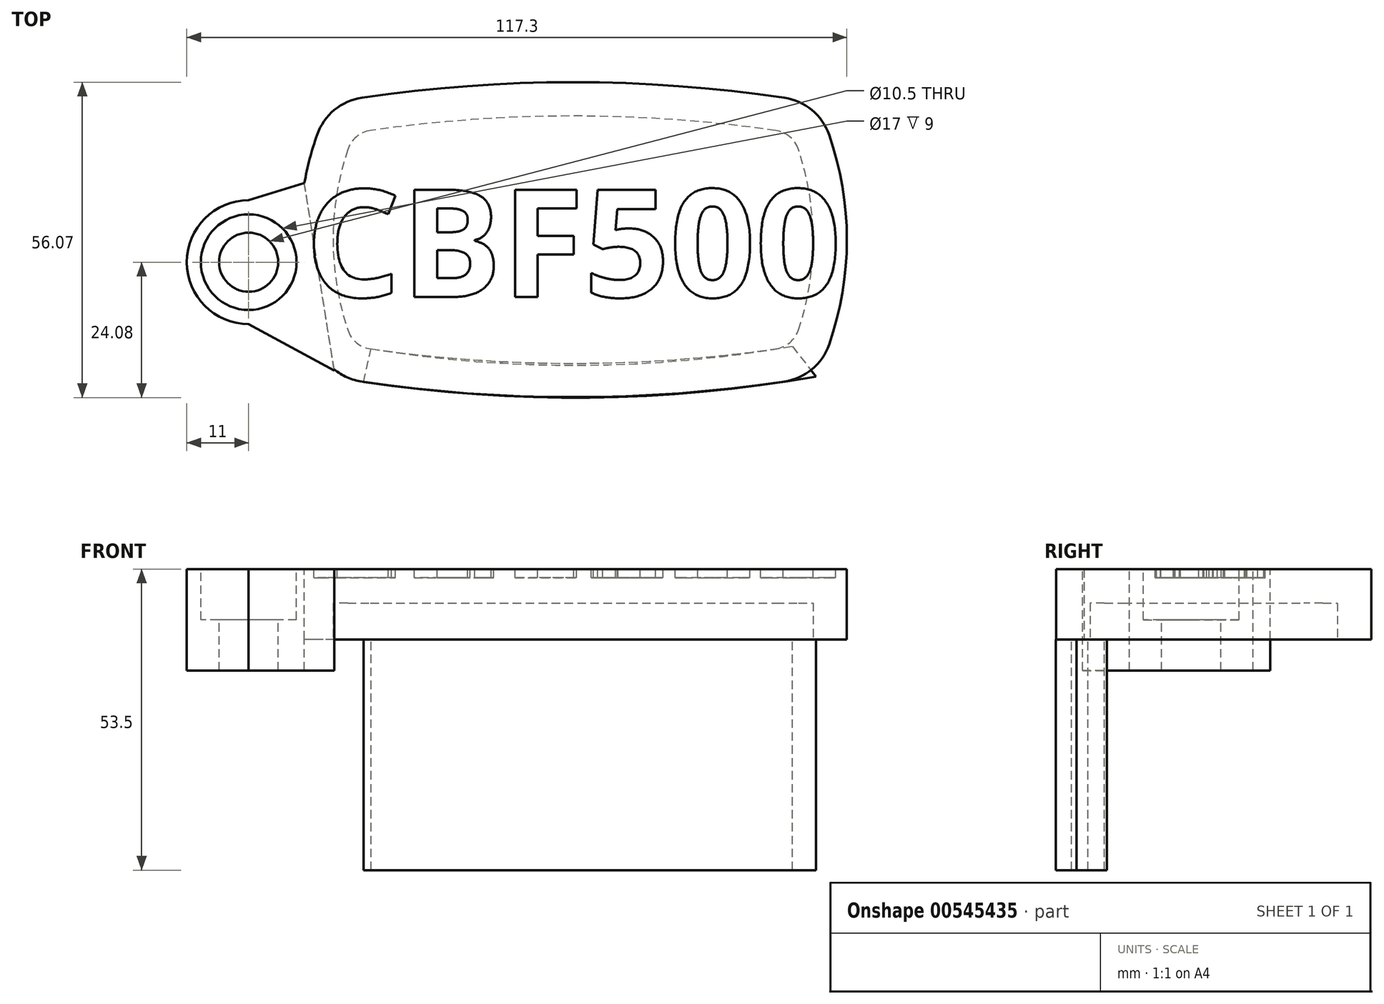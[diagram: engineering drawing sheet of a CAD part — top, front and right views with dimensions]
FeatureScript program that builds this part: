
annotation { "Feature Type Name" : "Feature", "Feature Type Description" : "" }
export const myFeature = defineFeature(function(context is Context, id is Id, definition is map)
    precondition{}
    {
        {
            var Q0;
            Q0=qCreatedBy(makeId("Top.planeOp"),FACE);
            var sketch = newSketch(context, id + "F0", { "sketchPlane" : qUnion([Q0])});
            skArc(sketch, "E0", {"start": v(0, 0) * mm, "mid": v(5.5, 24.35) * mm, "end": v(0, 48.7) * mm});
            skArc(sketch, "E1", {"start": v(-86.3, 0) * mm, "mid": v(-43.15, -3.64) * mm, "end": v(0, 0) * mm});
            skPoint(sketch, "E2", {"position": v(-43.15, 0) * mm});
            skPoint(sketch, "E3", {"position": v(0, 24.35) * mm});
            skLineSegment(sketch, "E4", {"start": v(-43.15, 0) * mm, "end": v(-43.15, 43.73) * mm, "construction": true});
            skLineSegment(sketch, "E5", {"start": v(0, 24.35) * mm, "end": v(-27.75, 24.35) * mm, "construction": true});
            skArc(sketch, "E6.MirrorCS", {"start": v(-86.3, 48.7) * mm, "mid": v(-43.15, 52.34) * mm, "end": v(0, 48.7) * mm});
            skArc(sketch, "E7.MirrorCS", {"start": v(-86.3, 0) * mm, "mid": v(-91.8, 24.35) * mm, "end": v(-86.3, 48.7) * mm});
            skSolve(sketch);
        }
        {
            var Q0;
            Q0 = qSketchRegion(id + "F0", true);
            extrude(context, id + "F1", {"entities" : qUnion([Q0]), "depth" : 12.5 * mm, "offsetDistance" : 25 * mm});
        }
        {
            var Q0;
            Q0=makeQuery(id+"F1.opExtrude","CAP_FACE",FACE,{"disambiguationData":[OSD([sQuery(id+"F0.wireOp",EDGE,"E0"),sQuery(id+"F0.wireOp",EDGE,"E1"),sQuery(id+"F0.wireOp",EDGE,"E6.MirrorCS"),sQuery(id+"F0.wireOp",EDGE,"E7.MirrorCS")])],"isStart":true});
            shell(context, id + "F2", {"entities" : qUnion([Q0]), "thickness" : 6 * mm});
        }
        {
            var Q0;
            Q0=makeQuery(id+"F1.opExtrude","CAP_FACE",FACE,{"disambiguationData":[OSD([sQuery(id+"F0.wireOp",EDGE,"E0"),sQuery(id+"F0.wireOp",EDGE,"E1"),sQuery(id+"F0.wireOp",EDGE,"E6.MirrorCS"),sQuery(id+"F0.wireOp",EDGE,"E7.MirrorCS")])],"isStart":true});
            var sketch = newSketch(context, id + "F3", { "sketchPlane" : qUnion([Q0])});
            skLineSegment(sketch, "E8", {"start": v(-4.18, -5.4) * mm, "end": v(0, 0) * mm});
            skLineSegment(sketch, "E9", {"start": v(-80.38, 0.94) * mm, "end": v(-79.02, -4.93) * mm});
            skArc(sketch, "E10", {"start": v(0, 0) * mm, "mid": v(-40.15, 3.72) * mm, "end": v(-80.38, 0.94) * mm});
            skArc(sketch, "E11", {"start": v(-4.18, -5.4) * mm, "mid": v(-41.58, -2.03) * mm, "end": v(-79.02, -4.93) * mm});
            skSolve(sketch);
        }
        {
            var Q0;
            Q0=makeQuery(id+"F1.opExtrude","SWEPT_EDGE",EDGE,{"disambiguationData":[OSD([sQuery(id+"F0.wireOp",EDGE,"E0"),sQuery(id+"F0.wireOp",EDGE,"E6.MirrorCS")])]});
            var Q1;
            Q1=makeQuery(id+"F1.opExtrude","SWEPT_EDGE",EDGE,{"disambiguationData":[OSD([sQuery(id+"F0.wireOp",EDGE,"E0"),sQuery(id+"F0.wireOp",EDGE,"E1")])]});
            var Q2;
            Q2=makeQuery(id+"F1.opExtrude","SWEPT_EDGE",EDGE,{"disambiguationData":[OSD([sQuery(id+"F0.wireOp",EDGE,"E1"),sQuery(id+"F0.wireOp",EDGE,"E7.MirrorCS")])]});
            var Q3;
            Q3=makeQuery(id+"F1.opExtrude","SWEPT_EDGE",EDGE,{"disambiguationData":[OSD([sQuery(id+"F0.wireOp",EDGE,"E6.MirrorCS"),sQuery(id+"F0.wireOp",EDGE,"E7.MirrorCS")])]});
            fillet(context, id + "F4", {"entities" : qUnion([Q0, Q1, Q2, Q3]), "radius" : 10 * mm, "tangentPropagation" : true, "allowEdgeOverflow" : false});
        }
        {
            var Q0;
            Q0 = qSketchRegion(id + "F3", true);
            extrude(context, id + "F5", {"entities" : qUnion([Q0]), "operationType" : NewBodyOperationType.ADD, "depth" : 31.6 * mm, "offsetDistance" : 25 * mm});
        }
        {
            var Q0;
            Q0=qCreatedBy(makeId("Front.planeOp"),FACE);
            var sketch = newSketch(context, id + "F6", { "sketchPlane" : qUnion([Q0])});
            skLineSegment(sketch, "E12", {"start": v(-60.38, -32) * mm, "end": v(-80.38, -32) * mm});
            skLineSegment(sketch, "E13", {"start": v(-80.38, -32) * mm, "end": v(-80.38, 0) * mm});
            skLineSegment(sketch, "E14", {"start": v(-80.38, 0) * mm, "end": v(-60.38, -32) * mm});
            skSolve(sketch);
        }
        {
            var Q0;
            Q0 = qSketchRegion(id + "F6", true);
            extrude(context, id + "F7", {"entities" : qUnion([Q0]), "operationType" : NewBodyOperationType.REMOVE, "oppositeDirection" : true, "depth" : 25 * mm, "offsetDistance" : 25 * mm, "hasSecondDirection" : true, "secondDirectionOppositeDirection" : false, "secondDirectionDepth" : 25 * mm});
        }
        {
            var Q0;
            Q0=makeQuery(id+"F5.opExtrude","SWEPT_EDGE",EDGE,{"disambiguationData":[OSD([sQuery(id+"F0.wireOp",EDGE,"E0"),sQuery(id+"F0.wireOp",EDGE,"E1"),sQuery(id+"F3.wireOp",EDGE,"E8"),sQuery(id+"F3.wireOp",EDGE,"2BGsfKZn-jyZl-Ejkt-ld0F-ZE4WbALv0zhB")])]});
            fillet(context, id + "F8", {"entities" : qUnion([Q0]), "radius" : 2 * mm, "tangentPropagation" : true, "allowEdgeOverflow" : false});
        }
        {
            var Q0;
            Q0=qCreatedBy(makeId("Front.planeOp"),FACE);
            var sketch = newSketch(context, id + "F9", { "sketchPlane" : qUnion([Q0])});
            skLineSegment(sketch, "E15", {"start": v(-1.05, -32) * mm, "end": v(-1.05, -16) * mm});
            skLineSegment(sketch, "E16", {"start": v(-1.05, -16) * mm, "end": v(-17.05, -32.07) * mm});
            skLineSegment(sketch, "E17", {"start": v(-17.05, -32.07) * mm, "end": v(-1.05, -32) * mm});
            skSolve(sketch);
        }
        {
            var Q0;
            Q0 = qSketchRegion(id + "F9", true);
            extrude(context, id + "F10", {"entities" : qUnion([Q0]), "operationType" : NewBodyOperationType.REMOVE, "oppositeDirection" : true, "depth" : 25 * mm, "offsetDistance" : 25 * mm, "hasSecondDirection" : true, "secondDirectionOppositeDirection" : false, "secondDirectionDepth" : 25 * mm});
        }
        {
            var Q0;
            Q0=makeQuery(id+"F1.opExtrude","CAP_FACE",FACE,{"disambiguationData":[OSD([sQuery(id+"F0.wireOp",EDGE,"E0"),sQuery(id+"F0.wireOp",EDGE,"E1"),sQuery(id+"F0.wireOp",EDGE,"E6.MirrorCS"),sQuery(id+"F0.wireOp",EDGE,"E7.MirrorCS")])],"isStart":false});
            var sketch = newSketch(context, id + "F11", { "sketchPlane" : qUnion([Q0])});
            skCircle(sketch, "E18", {"center": v(-100.8, 20.35) * mm, "radius": 5.25 * mm});
            skArc(sketch, "E19", {"start": v(-100.8, 31.35) * mm, "mid": v(-111.8, 20.35) * mm, "end": v(-100.8, 9.35) * mm});
            skLineSegment(sketch, "E20", {"start": v(-100.8, 31.35) * mm, "end": v(-90.9, 34.4) * mm});
            skLineSegment(sketch, "E21", {"start": v(-100.8, 9.35) * mm, "end": v(-85.57, 1.08) * mm});
            skPoint(sketch, "E21.endSnap0", {"position": v(-85.57, 1.3) * mm});
            skLineSegment(sketch, "E22", {"start": v(-85.57, 1.08) * mm, "end": v(-90.9, 34.4) * mm});
            skSolve(sketch);
        }
        {
            var Q0;
            Q0 = qSketchRegion(id + "F11", true);
            extrude(context, id + "F12", {"entities" : qUnion([Q0]), "operationType" : NewBodyOperationType.ADD, "oppositeDirection" : true, "depth" : 18 * mm, "offsetDistance" : 25 * mm});
        }
        {
            var Q0;
            Q0=makeQuery(id+"F12.boolean.opBoolean","MERGE",FACE,{"derivedFrom":[makeQuery(id+"F1.opExtrude","CAP_FACE",FACE,{"disambiguationData":[OSD([sQuery(id+"F0.wireOp",EDGE,"E0"),sQuery(id+"F0.wireOp",EDGE,"E1"),sQuery(id+"F0.wireOp",EDGE,"E6.MirrorCS"),sQuery(id+"F0.wireOp",EDGE,"E7.MirrorCS")])],"isStart":false}),makeQuery(id+"F12.opExtrude","CAP_FACE",FACE,{"disambiguationData":[OSD([sQuery(id+"F11.wireOp",EDGE,"E18"),sQuery(id+"F11.wireOp",EDGE,"E19"),sQuery(id+"F11.wireOp",EDGE,"E20"),sQuery(id+"F11.wireOp",EDGE,"Zz5zplqs-EO2A-KGeE-ttNv-1fYVzeMaVuvq"),sQuery(id+"F11.wireOp",EDGE,"bp7XOPkl-K0a4-XZaF-Fh4k-H6mTY0HdMkWh")])],"isStart":true})]});
            var sketch = newSketch(context, id + "F13", { "sketchPlane" : qUnion([Q0])});
            skCircle(sketch, "E23", {"center": v(-100.8, 20.35) * mm, "radius": 8.5 * mm});
            skSolve(sketch);
        }
        {
            var Q0;
            Q0 = qSketchRegion(id + "F13", true);
            extrude(context, id + "F14", {"entities" : qUnion([Q0]), "operationType" : NewBodyOperationType.REMOVE, "oppositeDirection" : true, "depth" : 9 * mm, "offsetDistance" : 25 * mm});
        }
        {
            var Q0;
            Q0=makeQuery(id+"F2.opShell","OFFSET_EDGE",EDGE,{"disambiguationData":[OSD([sQuery(id+"F0.wireOp",EDGE,"E0"),sQuery(id+"F0.wireOp",EDGE,"E6.MirrorCS")])]});
            var Q1;
            Q1=makeQuery(id+"F2.opShell","OFFSET_EDGE",EDGE,{"disambiguationData":[OSD([sQuery(id+"F0.wireOp",EDGE,"E6.MirrorCS"),sQuery(id+"F0.wireOp",EDGE,"E7.MirrorCS")])]});
            var Q2;
            Q2=makeQuery(id+"F2.opShell","OFFSET_EDGE",EDGE,{"disambiguationData":[OSD([sQuery(id+"F0.wireOp",EDGE,"E1"),sQuery(id+"F0.wireOp",EDGE,"E7.MirrorCS")])]});
            var Q3;
            Q3=makeQuery(id+"F2.opShell","OFFSET_EDGE",EDGE,{"disambiguationData":[OSD([sQuery(id+"F0.wireOp",EDGE,"E0"),sQuery(id+"F0.wireOp",EDGE,"E1")])]});
            fillet(context, id + "F15", {"entities" : qUnion([Q0, Q1, Q2, Q3]), "radius" : 5 * mm, "tangentPropagation" : true, "allowEdgeOverflow" : false});
        }
        {
            var Q0;
            Q0=makeQuery(id+"F12.boolean.opBoolean","MERGE",FACE,{"derivedFrom":[makeQuery(id+"F1.opExtrude","CAP_FACE",FACE,{"disambiguationData":[OSD([sQuery(id+"F0.wireOp",EDGE,"E0"),sQuery(id+"F0.wireOp",EDGE,"E1"),sQuery(id+"F0.wireOp",EDGE,"E6.MirrorCS"),sQuery(id+"F0.wireOp",EDGE,"E7.MirrorCS")])],"isStart":false}),makeQuery(id+"F12.opExtrude","CAP_FACE",FACE,{"disambiguationData":[OSD([sQuery(id+"F11.wireOp",EDGE,"E18"),sQuery(id+"F11.wireOp",EDGE,"E19"),sQuery(id+"F11.wireOp",EDGE,"E20"),sQuery(id+"F11.wireOp",EDGE,"E21"),sQuery(id+"F11.wireOp",EDGE,"E22")])],"isStart":true})]});
            var sketch = newSketch(context, id + "F16", { "sketchPlane" : qUnion([Q0])});
            skText(sketch, "E24", { "text": "CBF500", "fontName": "OpenSans-Bold.ttf"});
            const initialGuessF16  = {"E24": [-0.09075, 0.01418, 1, 0, 0.0192]};
            skSetInitialGuess(sketch, initialGuessF16);
            skSolve(sketch);
        }
        {
            var Q0;
            Q0 = qSketchRegion(id + "F16", true);
            extrude(context, id + "F17", {"entities" : qUnion([Q0]), "operationType" : NewBodyOperationType.REMOVE, "oppositeDirection" : true, "depth" : 1.5 * mm, "offsetDistance" : 25 * mm});
        }
        {
            var Q0;
            Q0 = qSketchRegion(id + "F3", true);
            extrude(context, id + "F18", {"entities" : qUnion([Q0]), "operationType" : NewBodyOperationType.ADD, "depth" : 41 * mm, "offsetDistance" : 25 * mm});
        }
    });
